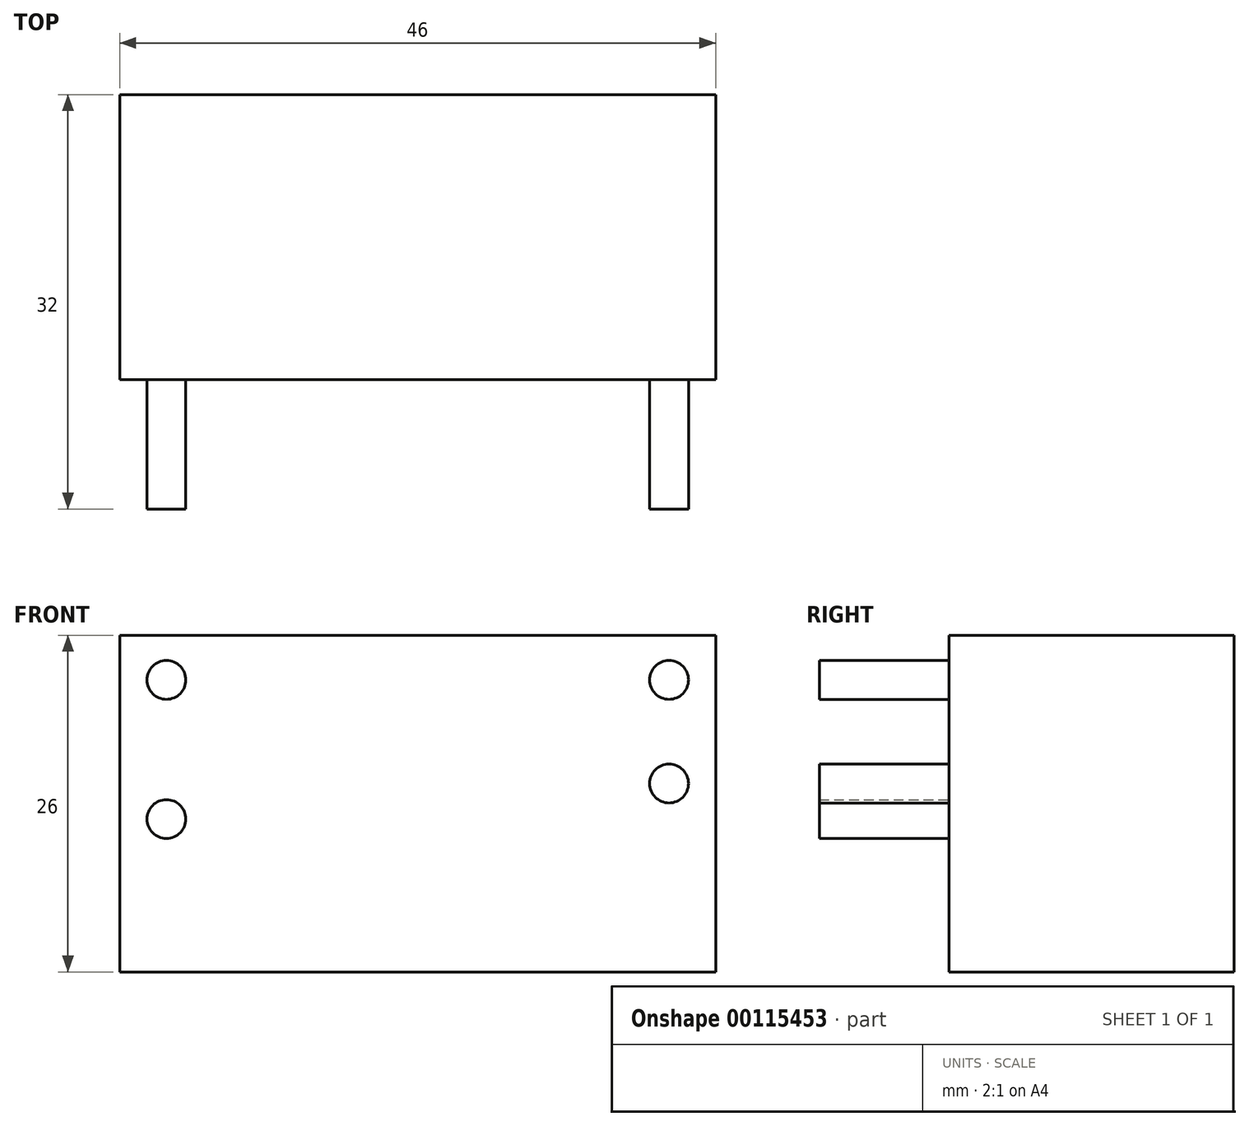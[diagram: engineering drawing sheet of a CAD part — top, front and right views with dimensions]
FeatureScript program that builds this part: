
annotation { "Feature Type Name" : "Feature", "Feature Type Description" : "" }
export const myFeature = defineFeature(function(context is Context, id is Id, definition is map)
    precondition{}
    {
        {
            var Q0;
            Q0=qCreatedBy(makeId("Front.planeOp"),FACE);
            var sketch = newSketch(context, id + "F0", { "sketchPlane" : qUnion([Q0])});
            skLineSegment(sketch, "E0.rect.bottom", {"start": v(23, 13) * mm, "end": v(-23, 13) * mm});
            skLineSegment(sketch, "E0.rect.top", {"start": v(23, -13) * mm, "end": v(-23, -13) * mm});
            skLineSegment(sketch, "E0.rect.left", {"start": v(23, 13) * mm, "end": v(23, -13) * mm});
            skLineSegment(sketch, "E0.rect.right", {"start": v(-23, 13) * mm, "end": v(-23, -13) * mm});
            skPoint(sketch, "E0.rect.middle", {"position": v(0, 0) * mm});
            skSolve(sketch);
        }
        {
            var Q0;
            Q0=qSketchRegion(id+"F0",true);
            extrude(context, id + "F1", {"entities" : qUnion([Q0]), "depth" : 22 * mm});
        }
        {
            var Q0;
            Q0=makeQuery(id+"F1.opExtrude","CAP_FACE",FACE,{"disambiguationData":[OSD([sQuery(id+"F0.wireOp",EDGE,"E0.rect.bottom"),sQuery(id+"F0.wireOp",EDGE,"E0.rect.top"),sQuery(id+"F0.wireOp",EDGE,"E0.rect.left"),sQuery(id+"F0.wireOp",EDGE,"E0.rect.right")])],"isStart":false});
            var sketch = newSketch(context, id + "F2", { "sketchPlane" : qUnion([Q0])});
            skCircle(sketch, "E1", {"center": v(-19.4, 9.55) * mm, "radius": 1.5 * mm});
            skCircle(sketch, "E2", {"center": v(-19.4, -1.2) * mm, "radius": 1.5 * mm});
            skCircle(sketch, "E3", {"center": v(19.4, 9.55) * mm, "radius": 1.5 * mm});
            skCircle(sketch, "E4", {"center": v(19.4, 1.55) * mm, "radius": 1.5 * mm});
            skLineSegment(sketch, "E5", {"start": v(-19.4, 9.55) * mm, "end": v(-19.4, -1.2) * mm, "construction": true});
            skLineSegment(sketch, "E6", {"start": v(19.4, 9.55) * mm, "end": v(19.4, 1.55) * mm, "construction": true});
            skSolve(sketch);
        }
        {
            var Q0;
            Q0=qSketchRegion(id+"F2",true);
            extrude(context, id + "F3", {"entities" : qUnion([Q0]), "operationType" : NewBodyOperationType.ADD, "depth" : 10 * mm});
        }
    });
